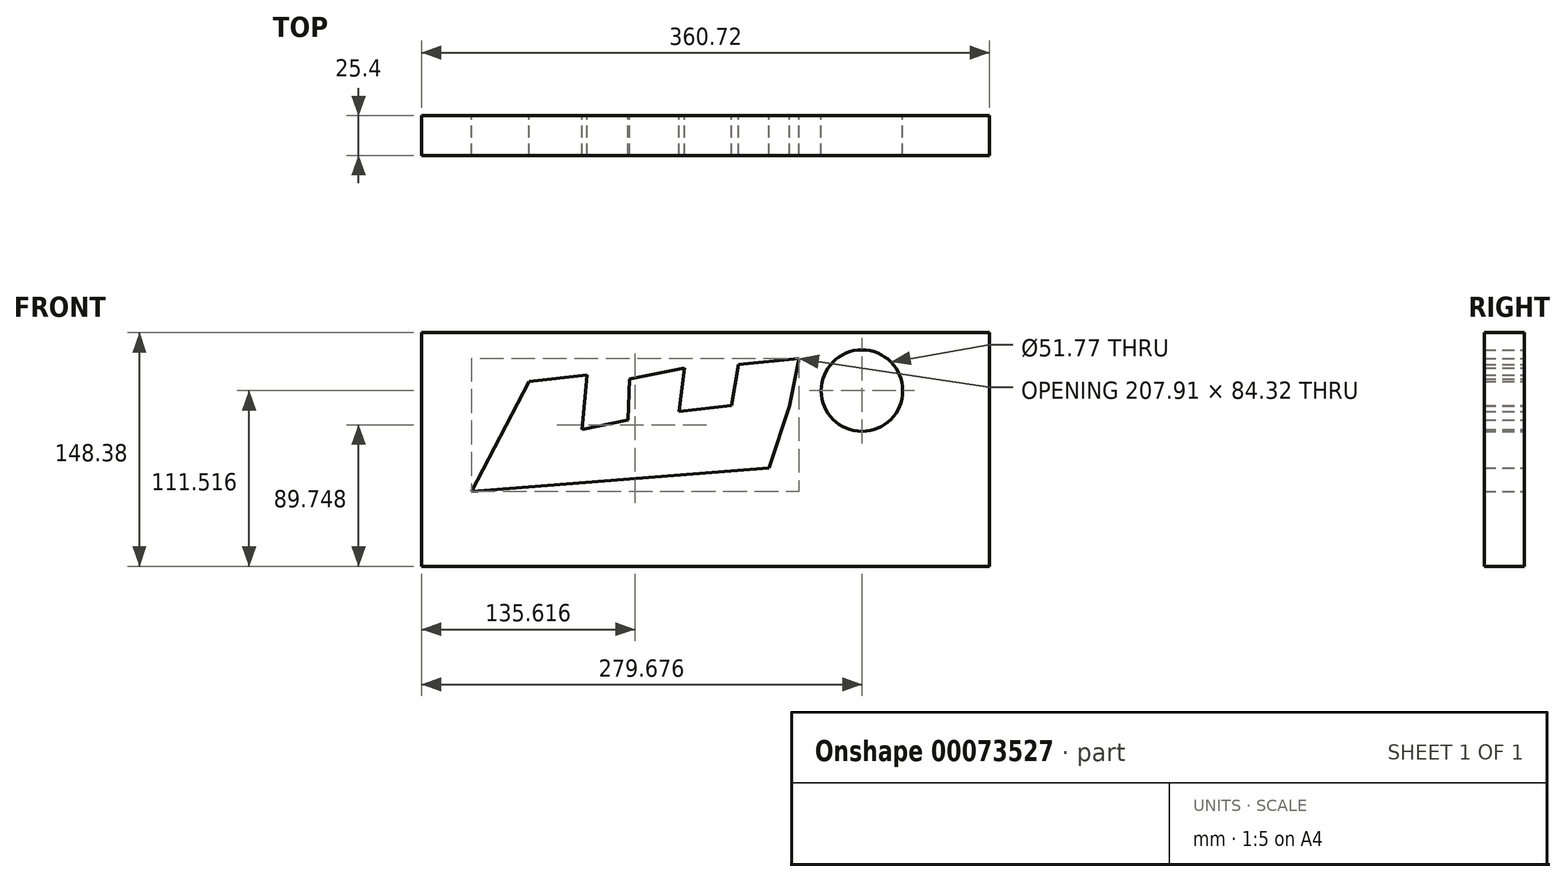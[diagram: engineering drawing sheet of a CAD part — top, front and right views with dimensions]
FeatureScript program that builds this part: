
annotation { "Feature Type Name" : "Feature", "Feature Type Description" : "" }
export const myFeature = defineFeature(function(context is Context, id is Id, definition is map)
    precondition{}
    {
        {
            var Q0;
            Q0=qCreatedBy(makeId("Front.planeOp"),FACE);
            var sketch = newSketch(context, id + "F0", { "sketchPlane" : qUnion([Q0])});
            skLineSegment(sketch, "E0.rect.bottom", {"start": v(-180.36, 74.19) * mm, "end": v(180.36, 74.19) * mm});
            skLineSegment(sketch, "E0.rect.top", {"start": v(-180.36, -74.19) * mm, "end": v(180.36, -74.19) * mm});
            skLineSegment(sketch, "E0.rect.left", {"start": v(-180.36, 74.19) * mm, "end": v(-180.36, -74.19) * mm});
            skLineSegment(sketch, "E0.rect.right", {"start": v(180.36, 74.19) * mm, "end": v(180.36, -74.19) * mm});
            skPoint(sketch, "E0.rect.middle", {"position": v(0, 0) * mm});
            skLineSegment(sketch, "E1", {"start": v(-112.25, 43.32) * mm, "end": v(-75.35, 47.23) * mm});
            skLineSegment(sketch, "E2", {"start": v(-75.35, 47.23) * mm, "end": v(-78.5, 12.57) * mm});
            skLineSegment(sketch, "E3", {"start": v(-78.5, 12.57) * mm, "end": v(-49.24, 18.76) * mm});
            skLineSegment(sketch, "E4", {"start": v(-49.24, 18.76) * mm, "end": v(-48.34, 44.67) * mm});
            skLineSegment(sketch, "E5", {"start": v(-48.34, 44.67) * mm, "end": v(-13.24, 51.65) * mm});
            skLineSegment(sketch, "E6", {"start": v(-13.24, 51.65) * mm, "end": v(-16.84, 24.06) * mm});
            skLineSegment(sketch, "E7", {"start": v(-16.84, 24.06) * mm, "end": v(16.46, 27.83) * mm});
            skLineSegment(sketch, "E8", {"start": v(16.46, 27.83) * mm, "end": v(20.96, 53.88) * mm});
            skLineSegment(sketch, "E9", {"start": v(20.96, 53.88) * mm, "end": v(59.2, 57.72) * mm});
            skLineSegment(sketch, "E10", {"start": v(59.2, 57.72) * mm, "end": v(53.36, 27.68) * mm});
            skLineSegment(sketch, "E11", {"start": v(53.36, 27.68) * mm, "end": v(40.3, -11.64) * mm});
            skLineSegment(sketch, "E12", {"start": v(40.3, -11.64) * mm, "end": v(-148.7, -26.6) * mm});
            skLineSegment(sketch, "E13", {"start": v(-148.7, -26.6) * mm, "end": v(-112.25, 43.32) * mm});
            skSolve(sketch);
        }
        {
            var Q0;
            Q0 = qSketchRegion(id + "F0", true);
            var Q1;
            Q1=makeQuery(id+"F0.imprint","IMPRINT",FACE,{"disambiguationData":[TD([[makeQuery(id+"F0.imprint","IMPRINT",EDGE,{"derivedFrom":sQuery(id+"F0.wireOp",EDGE,"E0.rect.bottom")}),-1.0]])]});
            extrude(context, id + "F1", {"entities" : qUnion([Q0, Q1]), "depth" : 25.4 * mm});
        }
        {
            var Q0;
            Q0=makeQuery(id+"F1.opExtrude","CAP_FACE",FACE,{"disambiguationData":[OSD([sQuery(id+"F0.wireOp",EDGE,"E0.rect.bottom"),sQuery(id+"F0.wireOp",EDGE,"E0.rect.top"),sQuery(id+"F0.wireOp",EDGE,"E0.rect.left"),sQuery(id+"F0.wireOp",EDGE,"E0.rect.right"),sQuery(id+"F0.wireOp",EDGE,"E1"),sQuery(id+"F0.wireOp",EDGE,"E2"),sQuery(id+"F0.wireOp",EDGE,"E3"),sQuery(id+"F0.wireOp",EDGE,"E4"),sQuery(id+"F0.wireOp",EDGE,"E5"),sQuery(id+"F0.wireOp",EDGE,"E6"),sQuery(id+"F0.wireOp",EDGE,"E7"),sQuery(id+"F0.wireOp",EDGE,"E8"),sQuery(id+"F0.wireOp",EDGE,"E9"),sQuery(id+"F0.wireOp",EDGE,"E10"),sQuery(id+"F0.wireOp",EDGE,"E11"),sQuery(id+"F0.wireOp",EDGE,"E12"),sQuery(id+"F0.wireOp",EDGE,"E13")])],"isStart":true});
            var sketch = newSketch(context, id + "F2", { "sketchPlane" : qUnion([Q0])});
            skCircle(sketch, "E14", {"center": v(-99.32, 37.33) * mm, "radius": 25.89 * mm});
            skSolve(sketch);
        }
        {
            var Q0;
            Q0 = qSketchRegion(id + "F2", true);
            extrude(context, id + "F3", {"entities" : qUnion([Q0]), "operationType" : NewBodyOperationType.REMOVE, "oppositeDirection" : true, "depth" : 25.4 * mm});
        }
    });
